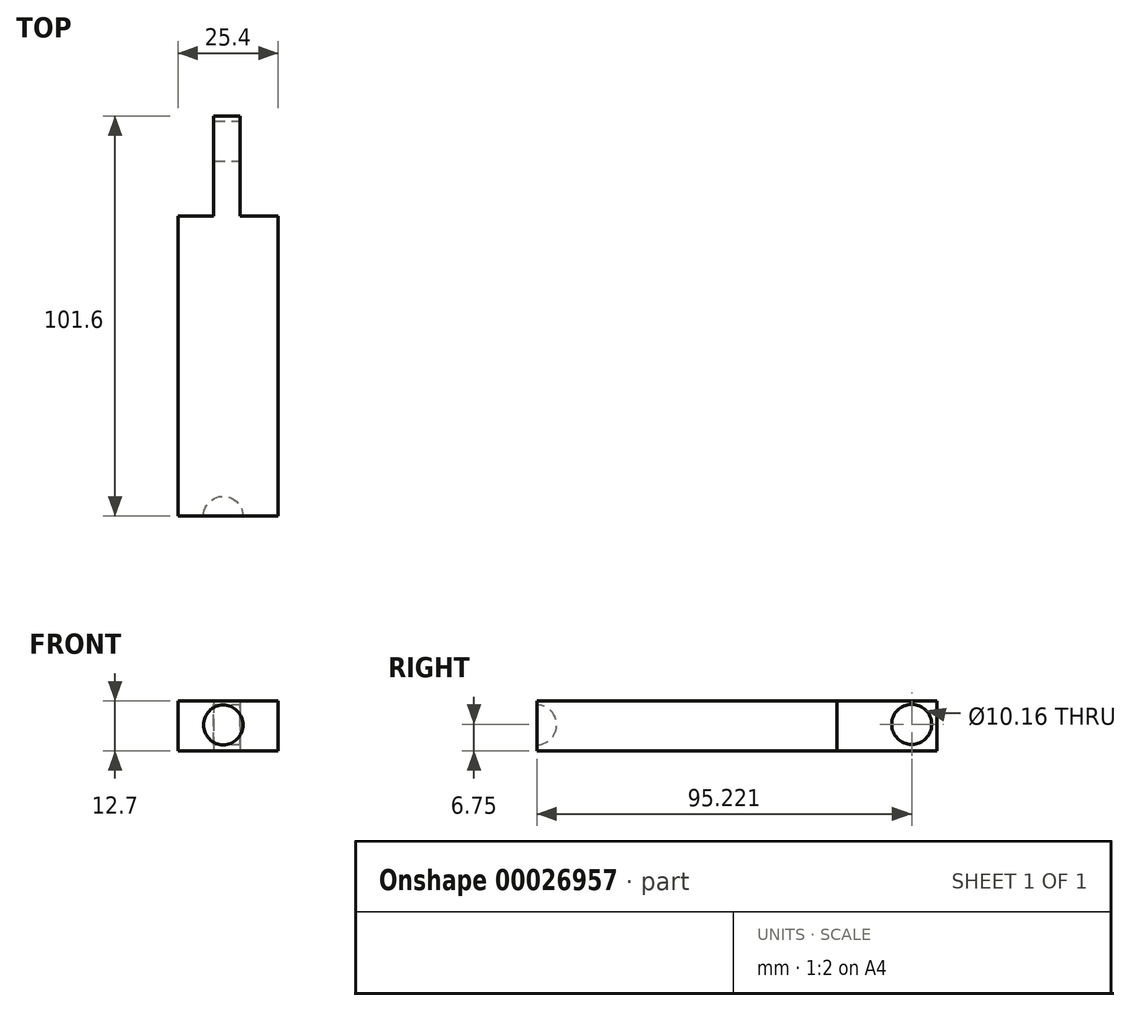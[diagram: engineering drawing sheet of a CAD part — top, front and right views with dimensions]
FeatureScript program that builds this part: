
annotation { "Feature Type Name" : "Feature", "Feature Type Description" : "" }
export const myFeature = defineFeature(function(context is Context, id is Id, definition is map)
    precondition{}
    {
        {
            var Q0;
            Q0=qCreatedBy(makeId("Front.planeOp"),FACE);
            var sketch = newSketch(context, id + "F0", { "sketchPlane" : qUnion([Q0])});
            skLineSegment(sketch, "E0.bottom", {"start": v(-14.49, 4.8) * mm, "end": v(10.91, 4.8) * mm});
            skLineSegment(sketch, "E0.top", {"start": v(-14.49, -7.9) * mm, "end": v(10.91, -7.9) * mm});
            skLineSegment(sketch, "E0.left", {"start": v(-14.49, 4.8) * mm, "end": v(-14.49, -7.9) * mm});
            skLineSegment(sketch, "E0.right", {"start": v(10.91, 4.8) * mm, "end": v(10.91, -7.9) * mm});
            skSolve(sketch);
        }
        {
            var Q0;
            Q0=makeQuery(id+"F0.imprint","IMPRINT",FACE,{"disambiguationData":[TD([[makeQuery(id+"F0.imprint","IMPRINT",EDGE,{"derivedFrom":sQuery(id+"F0.wireOp",EDGE,"E0.bottom")}),-1.0]])]});
            extrude(context, id + "F1", {"entities" : qUnion([Q0]), "depth" : 101.6 * mm});
        }
        {
            var Q0;
            Q0=makeQuery(id+"F1.opExtrude","CAP_FACE",FACE,{"disambiguationData":[OSD([sQuery(id+"F0.wireOp",EDGE,"E0.bottom"),sQuery(id+"F0.wireOp",EDGE,"E0.top"),sQuery(id+"F0.wireOp",EDGE,"E0.left"),sQuery(id+"F0.wireOp",EDGE,"E0.right")])],"isStart":false});
            var sketch = newSketch(context, id + "F2", { "sketchPlane" : qUnion([Q0])});
            skLineSegment(sketch, "E1", {"start": v(-3, 3.8) * mm, "end": v(-3, -6.37) * mm});
            skArc(sketch, "E2", {"start": v(-3, -6.37) * mm, "mid": v(2, -1.29) * mm, "end": v(-3, 3.8) * mm});
            skSolve(sketch);
        }
        {
            var Q0;
            Q0=makeQuery(id+"F2.imprint","IMPRINT",FACE,{"disambiguationData":[TD([[makeQuery(id+"F2.imprint","IMPRINT",EDGE,{"derivedFrom":sQuery(id+"F2.wireOp",EDGE,"E1")}),1.0]])]});
            var Q1;
            Q1=sQuery(id+"F2.wireOp",EDGE,"E1");
            revolve(context, id + "F3", {"operationType" : NewBodyOperationType.REMOVE, "entities" : qUnion([Q0]), "axis" : qUnion([Q1]), "revolveType" : RevolveType.FULL, "oppositeDirection" : true});
        }
        {
            var Q0;
            Q0=makeQuery(id+"F1.opExtrude","CAP_FACE",FACE,{"disambiguationData":[OSD([sQuery(id+"F0.wireOp",EDGE,"E0.bottom"),sQuery(id+"F0.wireOp",EDGE,"E0.top"),sQuery(id+"F0.wireOp",EDGE,"E0.left"),sQuery(id+"F0.wireOp",EDGE,"E0.right")])],"isStart":true});
            var sketch = newSketch(context, id + "F4", { "sketchPlane" : qUnion([Q0])});
            skLineSegment(sketch, "E3.bottom", {"start": v(-1.2, 4.8) * mm, "end": v(-10.91, 4.8) * mm});
            skLineSegment(sketch, "E3.top", {"start": v(-1.2, -7.9) * mm, "end": v(-10.91, -7.9) * mm});
            skLineSegment(sketch, "E3.left", {"start": v(-1.2, 4.8) * mm, "end": v(-1.2, -7.9) * mm});
            skLineSegment(sketch, "E3.right", {"start": v(-10.91, 4.8) * mm, "end": v(-10.91, -7.9) * mm});
            skLineSegment(sketch, "E4.bottom", {"start": v(14.49, 4.8) * mm, "end": v(5.51, 4.8) * mm});
            skLineSegment(sketch, "E4.top", {"start": v(14.49, -7.9) * mm, "end": v(5.51, -7.9) * mm});
            skLineSegment(sketch, "E4.left", {"start": v(14.49, 4.8) * mm, "end": v(14.49, -7.9) * mm});
            skLineSegment(sketch, "E4.right", {"start": v(5.51, 4.8) * mm, "end": v(5.51, -7.9) * mm});
            skSolve(sketch);
        }
        {
            var Q0;
            Q0=makeQuery(id+"F4.imprint","IMPRINT",FACE,{"disambiguationData":[TD([[makeQuery(id+"F4.imprint","IMPRINT",EDGE,{"derivedFrom":sQuery(id+"F4.wireOp",EDGE,"E3.bottom")}),1.0]])]});
            var Q1;
            Q1=makeQuery(id+"F4.imprint","IMPRINT",FACE,{"disambiguationData":[TD([[makeQuery(id+"F4.imprint","IMPRINT",EDGE,{"derivedFrom":sQuery(id+"F4.wireOp",EDGE,"E4.bottom")}),1.0]])]});
            extrude(context, id + "F5", {"entities" : qUnion([Q0, Q1]), "operationType" : NewBodyOperationType.REMOVE, "oppositeDirection" : true, "depth" : 25.4 * mm});
        }
        {
            var Q0;
            Q0=makeQuery(id+"F5.boolean.opBoolean","COPY",FACE,{"derivedFrom":makeQuery(id+"F5.opExtrude","SWEPT_FACE",FACE,{"disambiguationData":[OSD([sQuery(id+"F4.wireOp",EDGE,"E3.left")])]})});
            var sketch = newSketch(context, id + "F6", { "sketchPlane" : qUnion([Q0])});
            skCircle(sketch, "E5", {"center": v(-6.38, -1.14) * mm, "radius": 5.08 * mm});
            skSolve(sketch);
        }
        {
            var Q0;
            Q0=makeQuery(id+"F6.imprint","IMPRINT",FACE,{"disambiguationData":[TD([[makeQuery(id+"F6.imprint","IMPRINT",EDGE,{"derivedFrom":sQuery(id+"F6.wireOp",EDGE,"E5")}),1.0]])]});
            extrude(context, id + "F7", {"entities" : qUnion([Q0]), "operationType" : NewBodyOperationType.REMOVE, "oppositeDirection" : true, "depth" : 25.4 * mm});
        }
    });
